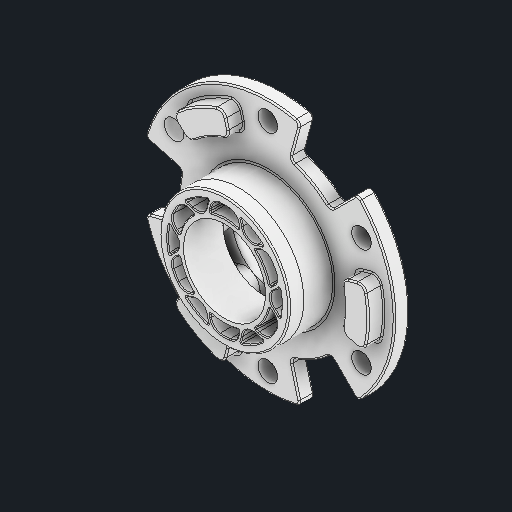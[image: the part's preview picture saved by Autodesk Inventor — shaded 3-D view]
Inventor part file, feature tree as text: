
AUTODESK INVENTOR PART (.ipt)
format: ipt  version: 2024 (Build 280153000, 153)  size: 883,200 bytes
history: native  units: in
note: dims shown in document units (in); Inventor stores cm internally (conversion verified against a paired STEP export)
features: fillet x1
ambient origin geometry x8: Origin, YZ Plane, XZ Plane, XY Plane, X Axis, Y Axis, Z Axis, Center Point
bodies: Solid1 (feature_tree)
feature tree (1):
  fillet  "Fillet27"  [1 undecoded]
note: 1 required parameter value undecoded (feature->parameter linkage not recoverable at this tier; creation-order binding heuristic only, values carry confidence <= 0.55)
